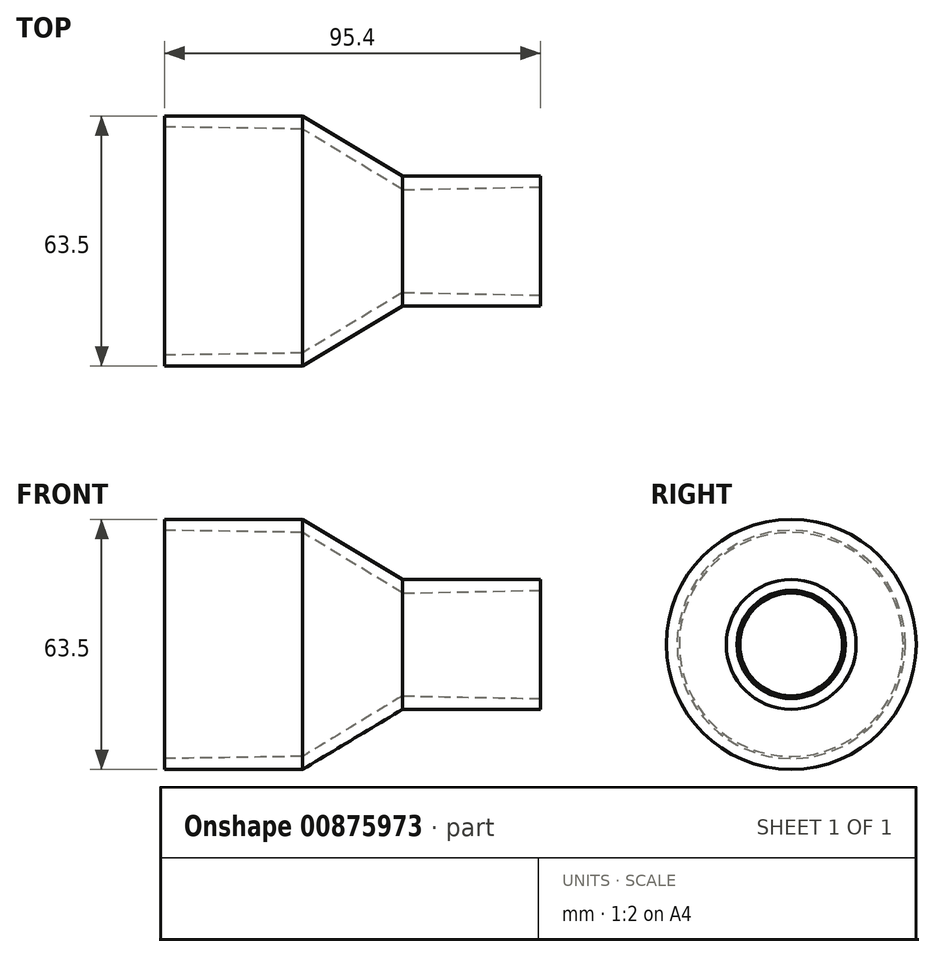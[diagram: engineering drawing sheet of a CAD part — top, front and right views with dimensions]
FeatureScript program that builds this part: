
annotation { "Feature Type Name" : "Feature", "Feature Type Description" : "" }
export const myFeature = defineFeature(function(context is Context, id is Id, definition is map)
    precondition{}
    {
        {
            var Q0;
            Q0=qCreatedBy(makeId("Front.planeOp"),FACE);
            var sketch = newSketch(context, id + "F0", { "sketchPlane" : qUnion([Q0])});
            skLineSegment(sketch, "E0", {"start": v(0, 0) * mm, "end": v(-90.9, 0) * mm, "construction": true});
            skLineSegment(sketch, "E1", {"start": v(0, 16.5) * mm, "end": v(35, 16.5) * mm});
            skLineSegment(sketch, "E2", {"start": v(35, 16.5) * mm, "end": v(35, 13.75) * mm});
            skLineSegment(sketch, "E3", {"start": v(35, 13.75) * mm, "end": v(0, 13.06) * mm});
            skLineSegment(sketch, "E4", {"start": v(0, 13.06) * mm, "end": v(-25.4, 28.45) * mm});
            skLineSegment(sketch, "E5", {"start": v(-25.4, 28.45) * mm, "end": v(-60.4, 29) * mm});
            skLineSegment(sketch, "E6", {"start": v(-60.4, 29) * mm, "end": v(-60.4, 31.75) * mm});
            skLineSegment(sketch, "E7", {"start": v(-60.4, 31.75) * mm, "end": v(-25.4, 31.75) * mm});
            skLineSegment(sketch, "E8", {"start": v(-25.4, 31.75) * mm, "end": v(0, 16.5) * mm});
            skPoint(sketch, "E9", {"position": v(9.6, 13.25) * mm});
            skPoint(sketch, "E10", {"position": v(-35, 28.6) * mm});
            skLineSegment(sketch, "E11", {"start": v(-25.4, 28.45) * mm, "end": v(-25.4, 31.75) * mm, "construction": true});
            skSolve(sketch);
        }
        {
            var Q0;
            Q0=qSketchRegion(id+"F0",true);
            var Q1;
            Q1=sQuery(id+"F0.wireOp",EDGE,"E0");
            revolve(context, id + "F1", {"surfaceOperationType" : NewSurfaceOperationType.NEW, "entities" : qUnion([Q0]), "axis" : qUnion([Q1]), "revolveType" : RevolveType.FULL});
        }
    });
